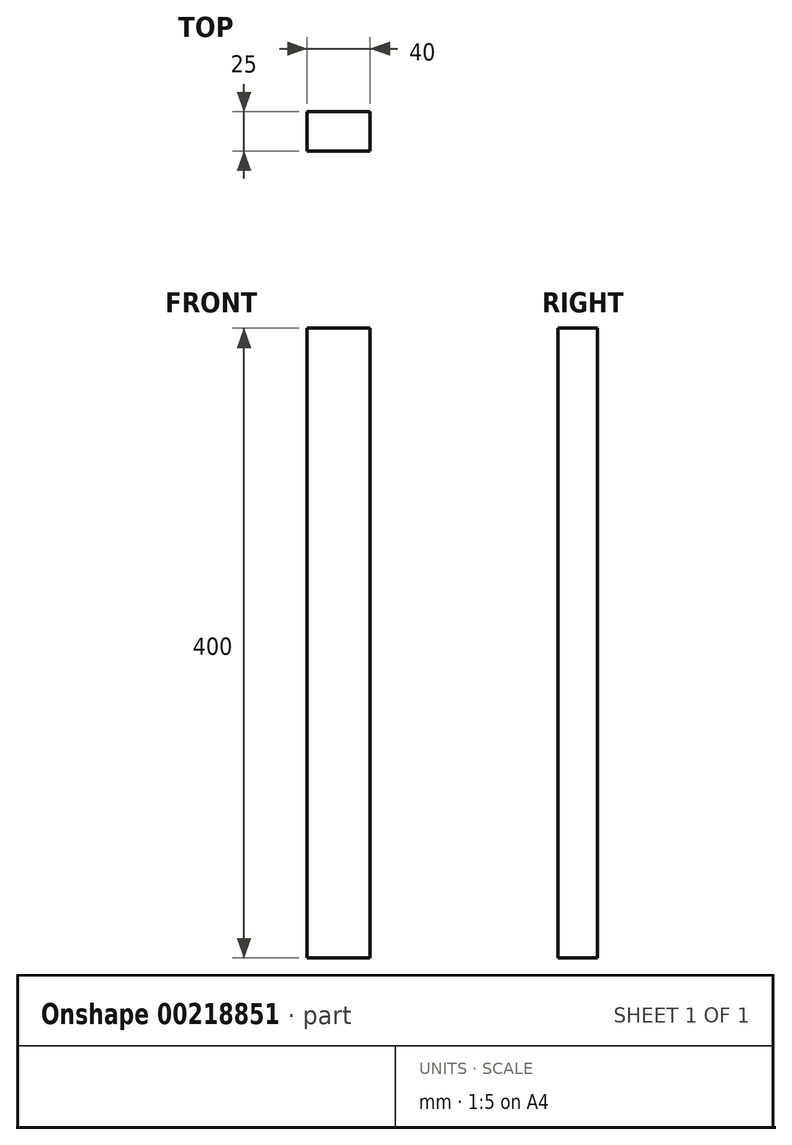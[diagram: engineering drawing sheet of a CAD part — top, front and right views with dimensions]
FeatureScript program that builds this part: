
annotation { "Feature Type Name" : "Feature", "Feature Type Description" : "" }
export const myFeature = defineFeature(function(context is Context, id is Id, definition is map)
    precondition{}
    {
        {
            var Q0;
            Q0=qCreatedBy(makeId("Front.planeOp"),FACE);
            var sketch = newSketch(context, id + "F0", { "sketchPlane" : qUnion([Q0])});
            skLineSegment(sketch, "E0.bottom", {"start": v(-62.5, -194.64) * mm, "end": v(-102.5, -194.64) * mm});
            skLineSegment(sketch, "E0.top", {"start": v(-62.5, 205.36) * mm, "end": v(-102.5, 205.36) * mm});
            skLineSegment(sketch, "E0.left", {"start": v(-62.5, -194.64) * mm, "end": v(-62.5, 205.36) * mm});
            skLineSegment(sketch, "E0.right", {"start": v(-102.5, -194.64) * mm, "end": v(-102.5, 205.36) * mm});
            skPoint(sketch, "E0.middle", {"position": v(-82.5, 5.36) * mm});
            skLineSegment(sketch, "E1.bottom", {"start": v(-62.5, 205.36) * mm, "end": v(497.5, 205.36) * mm});
            skLineSegment(sketch, "E1.top", {"start": v(-62.5, 186.36) * mm, "end": v(497.5, 186.36) * mm});
            skLineSegment(sketch, "E1.left", {"start": v(-62.5, 205.36) * mm, "end": v(-62.5, 186.36) * mm});
            skLineSegment(sketch, "E1.right", {"start": v(497.5, 205.36) * mm, "end": v(497.5, 186.36) * mm});
            skLineSegment(sketch, "E2.bottom", {"start": v(497.5, 205.36) * mm, "end": v(537.5, 205.36) * mm});
            skLineSegment(sketch, "E2.top", {"start": v(497.5, -194.64) * mm, "end": v(537.5, -194.64) * mm});
            skLineSegment(sketch, "E2.left", {"start": v(497.5, 205.36) * mm, "end": v(497.5, -194.64) * mm});
            skLineSegment(sketch, "E2.right", {"start": v(537.5, 205.36) * mm, "end": v(537.5, -194.64) * mm});
            skSolve(sketch);
        }
        {
            var Q0;
            Q0=makeQuery(id+"F0.imprint","IMPRINT",FACE,{"disambiguationData":[TD([[makeQuery(id+"F0.imprint","IMPRINT",EDGE,{"derivedFrom":sQuery(id+"F0.wireOp",EDGE,"E0.bottom")}),-1.0]])]});
            extrude(context, id + "F1", {"entities" : qUnion([Q0]), "depth" : 25 * mm});
        }
    });
